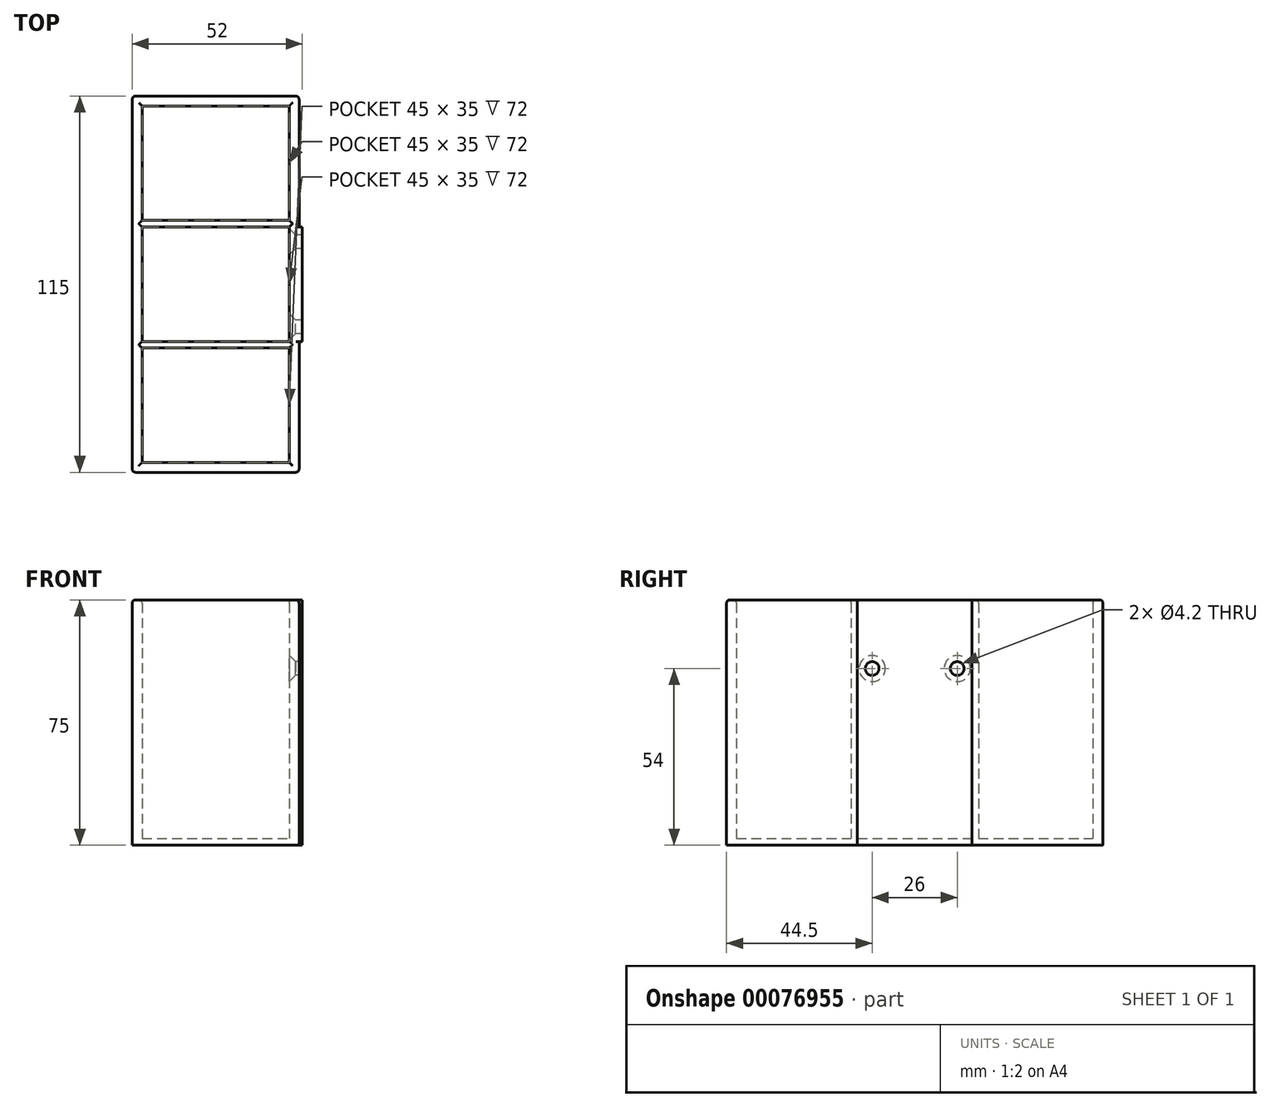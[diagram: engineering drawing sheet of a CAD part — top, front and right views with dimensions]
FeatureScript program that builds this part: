
annotation { "Feature Type Name" : "Feature", "Feature Type Description" : "" }
export const myFeature = defineFeature(function(context is Context, id is Id, definition is map)
    precondition{}
    {
        {
            var Q0;
            Q0=qCreatedBy(makeId("Top.planeOp"),FACE);
            var sketch = newSketch(context, id + "F0", { "sketchPlane" : qUnion([Q0])});
            skLineSegment(sketch, "E0.bottom", {"start": v(-54.6, -47.74) * mm, "end": v(-9.6, -47.74) * mm});
            skLineSegment(sketch, "E0.top", {"start": v(-54.6, 61.26) * mm, "end": v(-9.6, 61.26) * mm});
            skLineSegment(sketch, "E0.left", {"start": v(-54.6, -47.74) * mm, "end": v(-54.6, 61.26) * mm});
            skLineSegment(sketch, "E0.right", {"start": v(-9.6, -47.74) * mm, "end": v(-9.6, 61.26) * mm});
            skLineSegment(sketch, "E1", {"start": v(-54.6, 26.26) * mm, "end": v(-9.6, 26.26) * mm});
            skLineSegment(sketch, "E2", {"start": v(-9.6, 24.26) * mm, "end": v(-54.6, 24.26) * mm});
            skLineSegment(sketch, "E3", {"start": v(-54.6, -10.74) * mm, "end": v(-9.6, -10.74) * mm});
            skLineSegment(sketch, "E4.0", {"start": v(-57.6, 64.26) * mm, "end": v(-6.6, 64.26) * mm});
            skLineSegment(sketch, "E4.1", {"start": v(-57.6, -50.74) * mm, "end": v(-57.6, 64.26) * mm});
            skLineSegment(sketch, "E4.2", {"start": v(-57.6, -50.74) * mm, "end": v(-6.6, -50.74) * mm});
            skLineSegment(sketch, "E4.3", {"start": v(-6.6, -50.74) * mm, "end": v(-6.6, 64.26) * mm});
            skLineSegment(sketch, "E5", {"start": v(-54.6, -12.74) * mm, "end": v(-9.6, -12.74) * mm});
            skLineSegment(sketch, "E6", {"start": v(-6.6, -10.74) * mm, "end": v(-5.6, -10.74) * mm});
            skLineSegment(sketch, "E7", {"start": v(-5.6, -10.74) * mm, "end": v(-5.6, 24.26) * mm});
            skLineSegment(sketch, "E8", {"start": v(-5.6, 24.26) * mm, "end": v(-6.6, 24.26) * mm});
            skSolve(sketch);
        }
        {
            var Q0;
            {var subQ1=sQuery(id+"F0.wireOp",EDGE,"E0.bottom");Q0=makeQuery(id+"F0.imprint","IMPRINT",FACE,{"disambiguationData":[TD([[makeQuery(id+"F0.imprint","IMPRINT",EDGE,{"derivedFrom":subQ1}),-1.0]])]});}
            var Q1;
            {var subQ0=sQuery(id+"F0.wireOp",EDGE,"E1");Q1=makeQuery(id+"F0.imprint","IMPRINT",FACE,{"disambiguationData":[TD([[makeQuery(id+"F0.imprint","IMPRINT",EDGE,{"derivedFrom":subQ0}),-1.0]])]});}
            var Q2;
            {var subQ0=sQuery(id+"F0.wireOp",EDGE,"E3");Q2=makeQuery(id+"F0.imprint","IMPRINT",FACE,{"disambiguationData":[TD([[makeQuery(id+"F0.imprint","IMPRINT",EDGE,{"derivedFrom":subQ0}),-1.0]])]});}
            var Q3;
            {var subQ0=sQuery(id+"F0.wireOp",EDGE,"E6");Q3=makeQuery(id+"F0.imprint","IMPRINT",FACE,{"disambiguationData":[TD([[makeQuery(id+"F0.imprint","IMPRINT",EDGE,{"derivedFrom":subQ0}),1.0]])]});}
            extrude(context, id + "F1", {"entities" : qUnion([Q0, Q1, Q2, Q3]), "depth" : 75 * mm});
        }
        {
            var Q0;
            {var subQ0=sQuery(id+"F0.wireOp",EDGE,"E0.right");Q0=makeQuery(id+"F1.opExtrude","SWEPT_FACE",FACE,{"disambiguationData":[OSD([subQ0]),TDD([makeQuery(id+"F0.imprint","IMPRINT",EDGE,{"disambiguationData":[TD([[makeQuery(id+"F0.imprint","INTERSECT",VERTEX,{"derivedFrom":[subQ0,sQuery(id+"F0.wireOp",EDGE,"E2")]}),1.0]])],"derivedFrom":subQ0})])]});}
            var sketch = newSketch(context, id + "F2", { "sketchPlane" : qUnion([Q0])});
            skLineSegment(sketch, "E9", {"start": v(-6.76, 75) * mm, "end": v(-6.76, 0) * mm, "construction": true});
            skCircle(sketch, "E10", {"center": v(-6.76, 54) * mm, "radius": 13 * mm, "construction": true});
            skCircle(sketch, "E11", {"center": v(-19.76, 54) * mm, "radius": 1.6 * mm, "construction": true});
            skCircle(sketch, "E12", {"center": v(6.24, 54) * mm, "radius": 1.6 * mm, "construction": true});
            skSolve(sketch);
        }
        {
            var Q0;
            Q0=sQuery(id+"F2.wireOp",VERTEX,"E11.center");
            var Q1;
            Q1=sQuery(id+"F2.wireOp",VERTEX,"E12.center");
            var Q2;
            Q2=makeQuery(id+"F1.opExtrude","SWEPT_BODY",BODY,{"disambiguationData":[OSD([sQuery(id+"F0.wireOp",EDGE,"E0.bottom"),sQuery(id+"F0.wireOp",EDGE,"E0.top"),sQuery(id+"F0.wireOp",EDGE,"E0.left"),sQuery(id+"F0.wireOp",EDGE,"E0.right"),sQuery(id+"F0.wireOp",EDGE,"E1"),sQuery(id+"F0.wireOp",EDGE,"E2"),sQuery(id+"F0.wireOp",EDGE,"E3"),sQuery(id+"F0.wireOp",EDGE,"E4.0"),sQuery(id+"F0.wireOp",EDGE,"E4.1"),sQuery(id+"F0.wireOp",EDGE,"E4.2"),sQuery(id+"F0.wireOp",EDGE,"E4.3"),sQuery(id+"F0.wireOp",EDGE,"E5"),sQuery(id+"F0.wireOp",EDGE,"E6"),sQuery(id+"F0.wireOp",EDGE,"E7"),sQuery(id+"F0.wireOp",EDGE,"E8")])]});
            hole(context, id + "F3", {"style" : HoleStyle.C_SINK, "endStyle" : HoleEndStyle.THROUGH, "holeDiameter" : 4.2 * mm, "cSinkDiameter" : 8 * mm, "cSinkAngle" : 90 * degree, "locations" : qUnion([Q0, Q1]), "scope" : qUnion([Q2]), "isTappedThrough" : true});
        }
        {
            var Q0;
            {var subQ0=sQuery(id+"F0.wireOp",EDGE,"E2");Q0=makeQuery(id+"F0.imprint","IMPRINT",FACE,{"disambiguationData":[TD([[makeQuery(id+"F0.imprint","IMPRINT",EDGE,{"derivedFrom":subQ0}),1.0]])]});}
            var Q1;
            {var subQ0=sQuery(id+"F0.wireOp",EDGE,"E0.top");Q1=makeQuery(id+"F0.imprint","IMPRINT",FACE,{"disambiguationData":[TD([[makeQuery(id+"F0.imprint","IMPRINT",EDGE,{"derivedFrom":subQ0}),-1.0]])]});}
            var Q2;
            {var subQ0=sQuery(id+"F0.wireOp",EDGE,"E0.bottom");Q2=makeQuery(id+"F0.imprint","IMPRINT",FACE,{"disambiguationData":[TD([[makeQuery(id+"F0.imprint","IMPRINT",EDGE,{"derivedFrom":subQ0}),1.0]])]});}
            extrude(context, id + "F4", {"entities" : qUnion([Q0, Q1, Q2]), "operationType" : NewBodyOperationType.ADD, "depth" : 2 * mm});
        }
        {
            var Q0;
            Q0=makeQuery(id+"F1.opExtrude","SWEPT_EDGE",EDGE,{"disambiguationData":[OSD([sQuery(id+"F0.wireOp",EDGE,"E4.0"),sQuery(id+"F0.wireOp",EDGE,"E4.3")])]});
            var Q1;
            Q1=makeQuery(id+"F1.opExtrude","SWEPT_EDGE",EDGE,{"disambiguationData":[OSD([sQuery(id+"F0.wireOp",EDGE,"E4.0"),sQuery(id+"F0.wireOp",EDGE,"E4.1")])]});
            var Q2;
            Q2=makeQuery(id+"F1.opExtrude","SWEPT_EDGE",EDGE,{"disambiguationData":[OSD([sQuery(id+"F0.wireOp",EDGE,"E4.1"),sQuery(id+"F0.wireOp",EDGE,"E4.2")])]});
            var Q3;
            Q3=makeQuery(id+"F1.opExtrude","SWEPT_EDGE",EDGE,{"disambiguationData":[OSD([sQuery(id+"F0.wireOp",EDGE,"E4.2"),sQuery(id+"F0.wireOp",EDGE,"E4.3")])]});
            var Q4;
            Q4=makeQuery(id+"F1.opExtrude","CAP_EDGE",EDGE,{"disambiguationData":[OSD([sQuery(id+"F0.wireOp",EDGE,"E4.2")])],"isStart":false});
            var Q5;
            {var subQ0=sQuery(id+"F0.wireOp",EDGE,"E4.3");Q5=makeQuery(id+"F1.opExtrude","CAP_EDGE",EDGE,{"disambiguationData":[OSD([subQ0]),TDD([makeQuery(id+"F0.imprint","IMPRINT",EDGE,{"disambiguationData":[TD([[makeQuery(id+"F0.imprint","INTERSECT",VERTEX,{"derivedFrom":[sQuery(id+"F0.wireOp",EDGE,"E4.2"),subQ0]}),-1.0]])],"derivedFrom":subQ0})])],"isStart":false});}
            var Q6;
            Q6=makeQuery(id+"F1.opExtrude","CAP_EDGE",EDGE,{"disambiguationData":[OSD([sQuery(id+"F0.wireOp",EDGE,"E0.bottom")])],"isStart":false});
            var Q7;
            {var subQ0=sQuery(id+"F0.wireOp",EDGE,"E0.right");Q7=makeQuery(id+"F1.opExtrude","CAP_EDGE",EDGE,{"disambiguationData":[OSD([subQ0]),TDD([makeQuery(id+"F0.imprint","IMPRINT",EDGE,{"disambiguationData":[TD([[makeQuery(id+"F0.imprint","INTERSECT",VERTEX,{"derivedFrom":[sQuery(id+"F0.wireOp",EDGE,"E0.bottom"),subQ0]}),-1.0]])],"derivedFrom":subQ0})])],"isStart":false});}
            var Q8;
            Q8=makeQuery(id+"F1.opExtrude","CAP_EDGE",EDGE,{"disambiguationData":[OSD([sQuery(id+"F0.wireOp",EDGE,"E5")])],"isStart":false});
            var Q9;
            {var subQ0=sQuery(id+"F0.wireOp",EDGE,"E0.left");Q9=makeQuery(id+"F1.opExtrude","CAP_EDGE",EDGE,{"disambiguationData":[OSD([subQ0]),TDD([makeQuery(id+"F0.imprint","IMPRINT",EDGE,{"disambiguationData":[TD([[makeQuery(id+"F0.imprint","INTERSECT",VERTEX,{"derivedFrom":[sQuery(id+"F0.wireOp",EDGE,"E0.bottom"),subQ0]}),-1.0]])],"derivedFrom":subQ0})])],"isStart":false});}
            var Q10;
            Q10=makeQuery(id+"F1.opExtrude","CAP_EDGE",EDGE,{"disambiguationData":[OSD([sQuery(id+"F0.wireOp",EDGE,"E4.1")])],"isStart":false});
            var Q11;
            Q11=makeQuery(id+"F1.opExtrude","CAP_EDGE",EDGE,{"disambiguationData":[OSD([sQuery(id+"F0.wireOp",EDGE,"E3")])],"isStart":false});
            var Q12;
            {var subQ0=sQuery(id+"F0.wireOp",EDGE,"E0.left");Q12=makeQuery(id+"F1.opExtrude","CAP_EDGE",EDGE,{"disambiguationData":[OSD([subQ0]),TDD([makeQuery(id+"F0.imprint","IMPRINT",EDGE,{"disambiguationData":[TD([[makeQuery(id+"F0.imprint","INTERSECT",VERTEX,{"derivedFrom":[subQ0,sQuery(id+"F0.wireOp",EDGE,"E2")]}),1.0]])],"derivedFrom":subQ0})])],"isStart":false});}
            var Q13;
            Q13=makeQuery(id+"F1.opExtrude","CAP_EDGE",EDGE,{"disambiguationData":[OSD([sQuery(id+"F0.wireOp",EDGE,"E2")])],"isStart":false});
            var Q14;
            Q14=makeQuery(id+"F1.opExtrude","CAP_EDGE",EDGE,{"disambiguationData":[OSD([sQuery(id+"F0.wireOp",EDGE,"E1")])],"isStart":false});
            var Q15;
            {var subQ0=sQuery(id+"F0.wireOp",EDGE,"E0.left");Q15=makeQuery(id+"F1.opExtrude","CAP_EDGE",EDGE,{"disambiguationData":[OSD([subQ0]),TDD([makeQuery(id+"F0.imprint","IMPRINT",EDGE,{"disambiguationData":[TD([[makeQuery(id+"F0.imprint","INTERSECT",VERTEX,{"derivedFrom":[sQuery(id+"F0.wireOp",EDGE,"E0.top"),subQ0]}),1.0]])],"derivedFrom":subQ0})])],"isStart":false});}
            var Q16;
            Q16=makeQuery(id+"F1.opExtrude","CAP_EDGE",EDGE,{"disambiguationData":[OSD([sQuery(id+"F0.wireOp",EDGE,"E4.0")])],"isStart":false});
            var Q17;
            Q17=makeQuery(id+"F1.opExtrude","CAP_EDGE",EDGE,{"disambiguationData":[OSD([sQuery(id+"F0.wireOp",EDGE,"E0.top")])],"isStart":false});
            var Q18;
            {var subQ0=sQuery(id+"F0.wireOp",EDGE,"E4.3");Q18=makeQuery(id+"F1.opExtrude","CAP_EDGE",EDGE,{"disambiguationData":[OSD([subQ0]),TDD([makeQuery(id+"F0.imprint","IMPRINT",EDGE,{"disambiguationData":[TD([[makeQuery(id+"F0.imprint","INTERSECT",VERTEX,{"derivedFrom":[sQuery(id+"F0.wireOp",EDGE,"E4.0"),subQ0]}),1.0]])],"derivedFrom":subQ0})])],"isStart":false});}
            var Q19;
            {var subQ0=sQuery(id+"F0.wireOp",EDGE,"E0.right");Q19=makeQuery(id+"F1.opExtrude","CAP_EDGE",EDGE,{"disambiguationData":[OSD([subQ0]),TDD([makeQuery(id+"F0.imprint","IMPRINT",EDGE,{"disambiguationData":[TD([[makeQuery(id+"F0.imprint","INTERSECT",VERTEX,{"derivedFrom":[sQuery(id+"F0.wireOp",EDGE,"E0.top"),subQ0]}),1.0]])],"derivedFrom":subQ0})])],"isStart":false});}
            var Q20;
            {var subQ0=sQuery(id+"F0.wireOp",EDGE,"E0.right");Q20=makeQuery(id+"F1.opExtrude","CAP_EDGE",EDGE,{"disambiguationData":[OSD([subQ0]),TDD([makeQuery(id+"F0.imprint","IMPRINT",EDGE,{"disambiguationData":[TD([[makeQuery(id+"F0.imprint","INTERSECT",VERTEX,{"derivedFrom":[subQ0,sQuery(id+"F0.wireOp",EDGE,"E2")]}),1.0]])],"derivedFrom":subQ0})])],"isStart":false});}
            fillet(context, id + "F5", {"entities" : qUnion([Q0, Q1, Q2, Q3, Q4, Q5, Q6, Q7, Q8, Q9, Q10, Q11, Q12, Q13, Q14, Q15, Q16, Q17, Q18, Q19, Q20]), "radius" : 1 * mm, "tangentPropagation" : true, "allowEdgeOverflow" : false});
        }
    });
